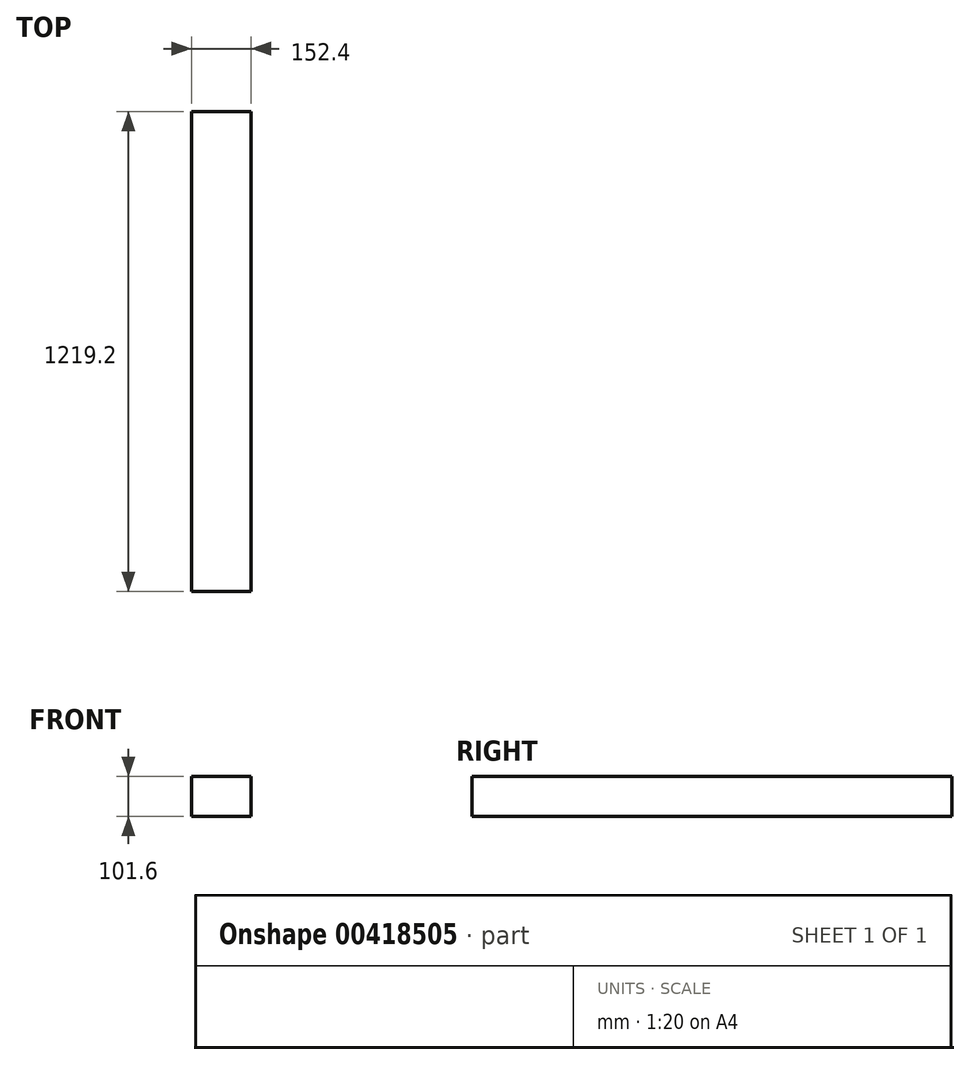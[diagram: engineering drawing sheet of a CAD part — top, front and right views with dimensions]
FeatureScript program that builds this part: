
annotation { "Feature Type Name" : "Feature", "Feature Type Description" : "" }
export const myFeature = defineFeature(function(context is Context, id is Id, definition is map)
    precondition{}
    {
        {
            var Q0;
            Q0=qCreatedBy(makeId("Front.planeOp"),FACE);
            var sketch = newSketch(context, id + "F0", { "sketchPlane" : qUnion([Q0])});
            skLineSegment(sketch, "E0.bottom", {"start": v(0, 0) * mm, "end": v(152.4, 0) * mm});
            skLineSegment(sketch, "E0.top", {"start": v(0, 101.6) * mm, "end": v(152.4, 101.6) * mm});
            skLineSegment(sketch, "E0.left", {"start": v(0, 0) * mm, "end": v(0, 101.6) * mm});
            skLineSegment(sketch, "E0.right", {"start": v(152.4, 0) * mm, "end": v(152.4, 101.6) * mm});
            skSolve(sketch);
        }
        {
            var Q0;
            Q0 = qSketchRegion(id + "F0", true);
            extrude(context, id + "F1", {"entities" : qUnion([Q0]), "oppositeDirection" : true, "depth" : 1219.2 * mm});
        }
    });
